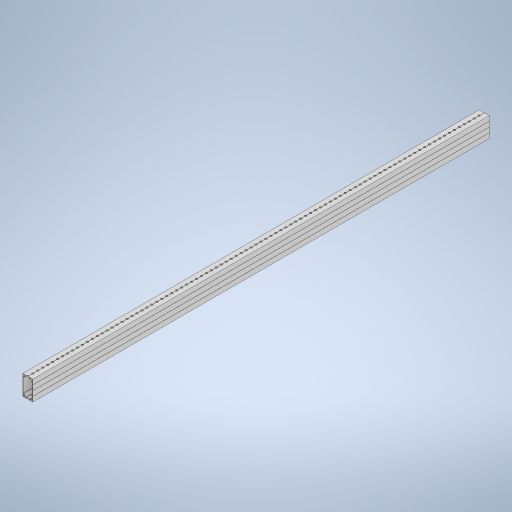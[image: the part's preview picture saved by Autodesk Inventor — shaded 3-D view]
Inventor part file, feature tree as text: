
AUTODESK INVENTOR PART (.ipt)
format: ipt  version: 2023 (Build 270158000, 158)  size: 977,920 bytes
history: native  units: in
note: dims shown in document units (in); Inventor stores cm internally (conversion verified against a paired STEP export)
features: extrude x1, sketch x1, other x1
ambient origin geometry x8: Origin, YZ Plane, XZ Plane, XY Plane, X Axis, Y Axis, Z Axis, Center Point
bodies: Solid1 (feature_tree)
feature tree (3):
  extrude  "Extrusion1"  [1 undecoded]
  sketch  "Sketch1"  dims[d0=1.0in d1=0.0in]
  other  "Scribe Line Pattern"
note: 1 required parameter value undecoded (feature->parameter linkage not recoverable at this tier; creation-order binding heuristic only, values carry confidence <= 0.55)
